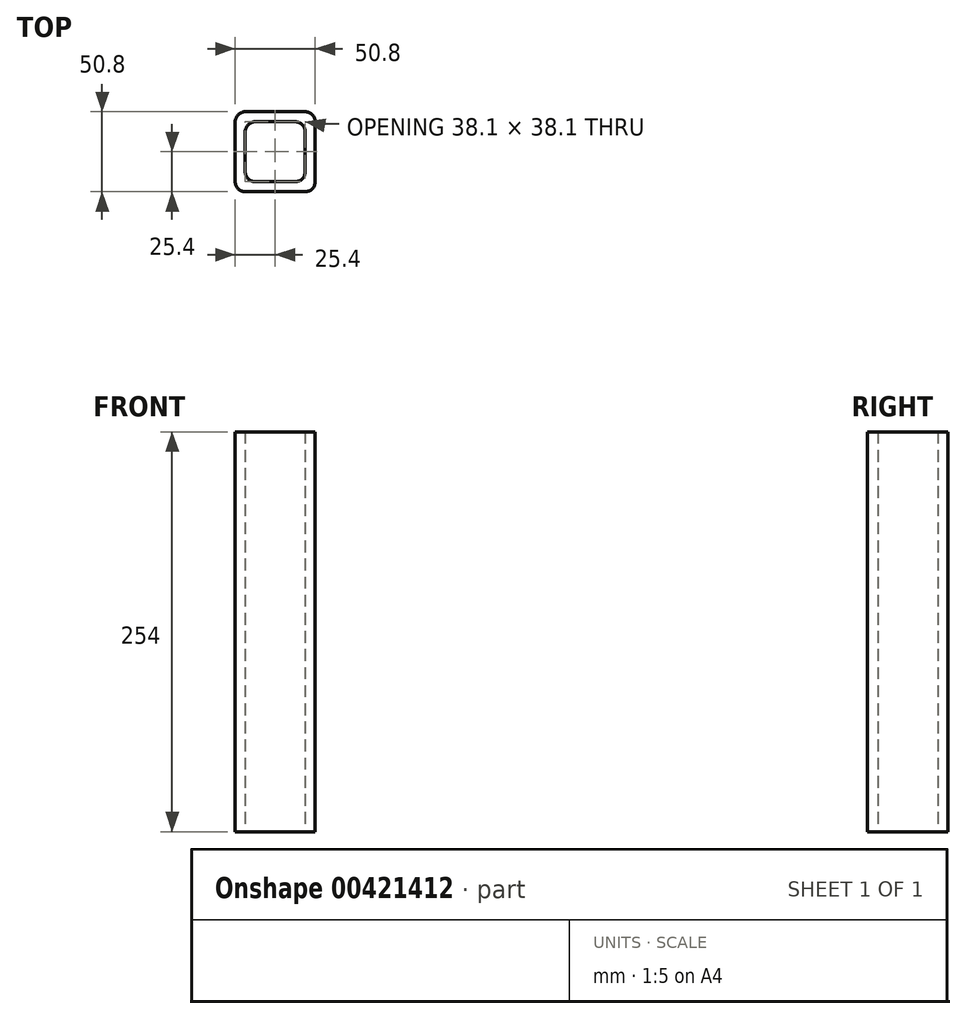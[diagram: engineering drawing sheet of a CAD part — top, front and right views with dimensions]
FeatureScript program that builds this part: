
annotation { "Feature Type Name" : "Feature", "Feature Type Description" : "" }
export const myFeature = defineFeature(function(context is Context, id is Id, definition is map)
    precondition{}
    {
        {
            var Q0;
            Q0=qCreatedBy(makeId("Top.planeOp"),FACE);
            var sketch = newSketch(context, id + "F0", { "sketchPlane" : qUnion([Q0])});
            skLineSegment(sketch, "E0.bottom", {"start": v(19.05, -19.05) * mm, "end": v(-19.05, -19.05) * mm});
            skLineSegment(sketch, "E0.top", {"start": v(19.05, 19.05) * mm, "end": v(-19.05, 19.05) * mm});
            skLineSegment(sketch, "E0.left", {"start": v(19.05, -19.05) * mm, "end": v(19.05, 19.05) * mm});
            skLineSegment(sketch, "E0.right", {"start": v(-19.05, -19.05) * mm, "end": v(-19.05, 19.05) * mm});
            skPoint(sketch, "E0.middle", {"position": v(0, 0) * mm});
            skLineSegment(sketch, "E1.bottom", {"start": v(25.4, -25.4) * mm, "end": v(-25.4, -25.4) * mm});
            skLineSegment(sketch, "E1.top", {"start": v(25.4, 25.4) * mm, "end": v(-25.4, 25.4) * mm});
            skLineSegment(sketch, "E1.left", {"start": v(25.4, -25.4) * mm, "end": v(25.4, 25.4) * mm});
            skLineSegment(sketch, "E1.right", {"start": v(-25.4, -25.4) * mm, "end": v(-25.4, 25.4) * mm});
            skSolve(sketch);
        }
        {
            var Q0;
            Q0 = qSketchRegion(id + "F0", true);
            extrude(context, id + "F1", {"entities" : qUnion([Q0]), "depth" : 254 * mm});
        }
        {
            var Q0;
            Q0=makeQuery(id+"F1.opExtrude","SWEPT_EDGE",EDGE,{"disambiguationData":[OSD([sQuery(id+"F0.wireOp",EDGE,"E1.top"),sQuery(id+"F0.wireOp",EDGE,"E1.right")])]});
            var Q1;
            Q1=makeQuery(id+"F1.opExtrude","SWEPT_EDGE",EDGE,{"disambiguationData":[OSD([sQuery(id+"F0.wireOp",EDGE,"E1.bottom"),sQuery(id+"F0.wireOp",EDGE,"E1.right")])]});
            var Q2;
            Q2=makeQuery(id+"F1.opExtrude","SWEPT_EDGE",EDGE,{"disambiguationData":[OSD([sQuery(id+"F0.wireOp",EDGE,"E0.bottom"),sQuery(id+"F0.wireOp",EDGE,"E0.left")])]});
            var Q3;
            Q3=makeQuery(id+"F1.opExtrude","SWEPT_EDGE",EDGE,{"disambiguationData":[OSD([sQuery(id+"F0.wireOp",EDGE,"E1.top"),sQuery(id+"F0.wireOp",EDGE,"E1.left")])]});
            var Q4;
            Q4=makeQuery(id+"F1.opExtrude","SWEPT_EDGE",EDGE,{"disambiguationData":[OSD([sQuery(id+"F0.wireOp",EDGE,"E0.bottom"),sQuery(id+"F0.wireOp",EDGE,"E0.right")])]});
            var Q5;
            Q5=makeQuery(id+"F1.opExtrude","SWEPT_EDGE",EDGE,{"disambiguationData":[OSD([sQuery(id+"F0.wireOp",EDGE,"E0.top"),sQuery(id+"F0.wireOp",EDGE,"E0.right")])]});
            var Q6;
            Q6=makeQuery(id+"F1.opExtrude","SWEPT_EDGE",EDGE,{"disambiguationData":[OSD([sQuery(id+"F0.wireOp",EDGE,"E0.top"),sQuery(id+"F0.wireOp",EDGE,"E0.left")])]});
            fillet(context, id + "F2", {"entities" : qUnion([Q0, Q1, Q2, Q3, Q4, Q5, Q6]), "radius" : 6.35 * mm, "tangentPropagation" : true, "allowEdgeOverflow" : false});
        }
        {
            var Q0;
            Q0=makeQuery(id+"F1.opExtrude","SWEPT_EDGE",EDGE,{"disambiguationData":[OSD([sQuery(id+"F0.wireOp",EDGE,"E1.bottom"),sQuery(id+"F0.wireOp",EDGE,"E1.left")])]});
            fillet(context, id + "F3", {"entities" : qUnion([Q0]), "radius" : 6.35 * mm, "tangentPropagation" : true, "allowEdgeOverflow" : false});
        }
    });
